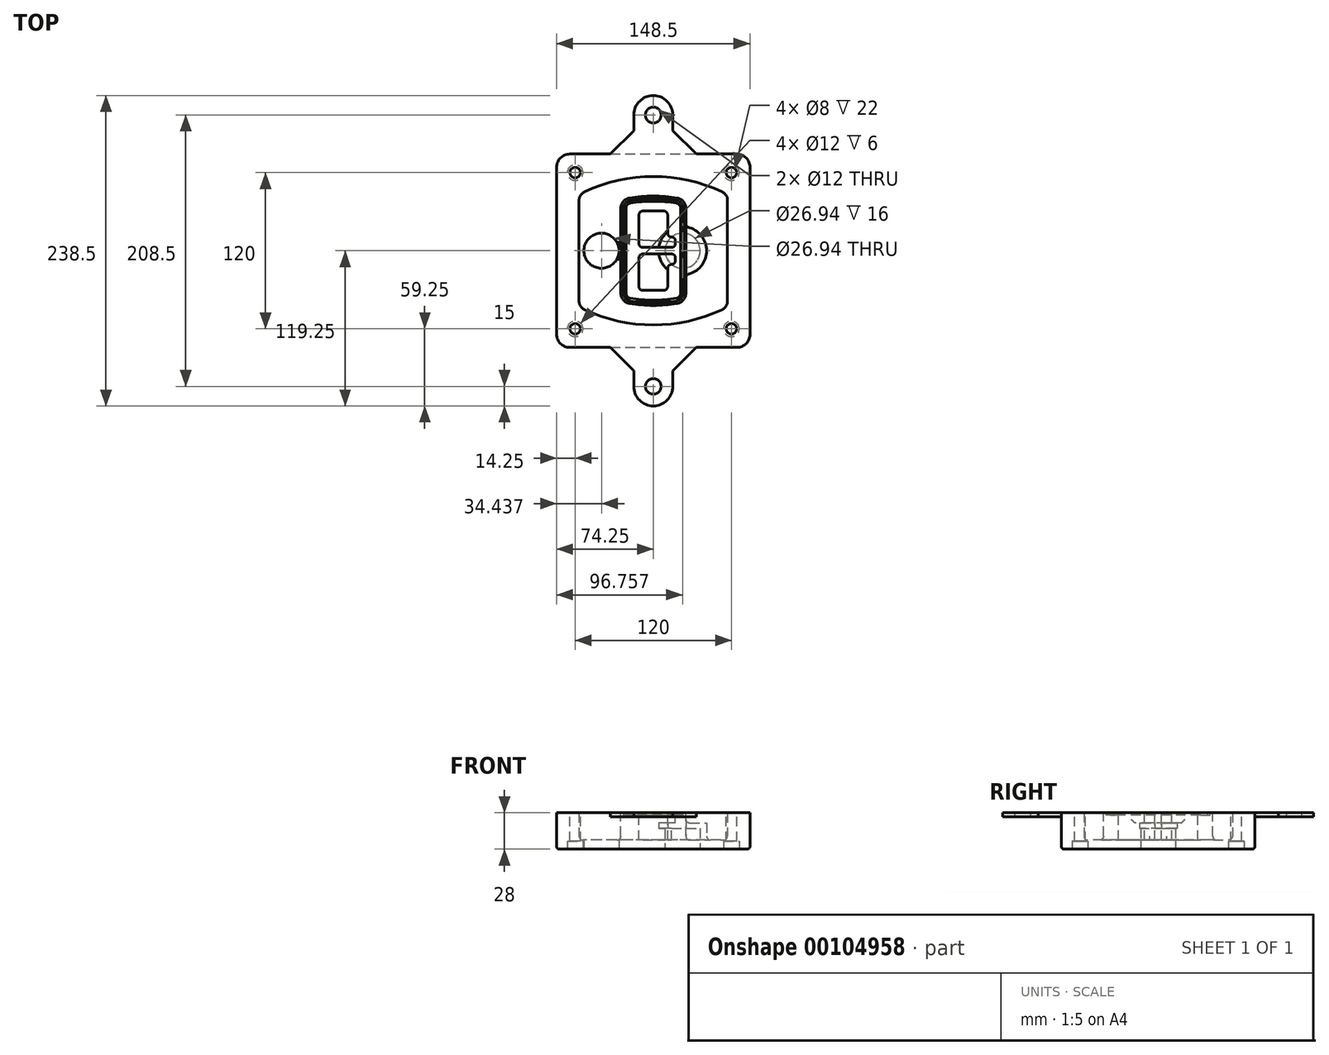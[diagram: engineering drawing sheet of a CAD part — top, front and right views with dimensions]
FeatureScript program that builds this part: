
annotation { "Feature Type Name" : "Feature", "Feature Type Description" : "" }
export const myFeature = defineFeature(function(context is Context, id is Id, definition is map)
    precondition{}
    {
        {
            var Q0;
            Q0=qCreatedBy(makeId("Top.planeOp"),FACE);
            var sketch = newSketch(context, id + "F0", { "sketchPlane" : qUnion([Q0])});
            skPoint(sketch, "E0.rect.middle", {"position": v(0, 0) * mm});
            skLineSegment(sketch, "E1.bottom", {"start": v(-64.25, -74.25) * mm, "end": v(64.25, -74.25) * mm});
            skLineSegment(sketch, "E1.top", {"start": v(-64.25, 74.25) * mm, "end": v(64.25, 74.25) * mm});
            skLineSegment(sketch, "E1.left", {"start": v(-74.25, -64.25) * mm, "end": v(-74.25, 64.25) * mm});
            skLineSegment(sketch, "E1.right", {"start": v(74.25, -64.25) * mm, "end": v(74.25, 64.25) * mm});
            skLineSegment(sketch, "E2", {"start": v(-74.25, 74.25) * mm, "end": v(74.25, -74.25) * mm, "construction": true});
            skLineSegment(sketch, "E3", {"start": v(74.25, 74.25) * mm, "end": v(-74.25, -74.25) * mm, "construction": true});
            skCircle(sketch, "E4", {"center": v(-60, 60) * mm, "radius": 4 * mm});
            skCircle(sketch, "E5", {"center": v(60, 60) * mm, "radius": 4 * mm});
            skCircle(sketch, "E6", {"center": v(60, -60) * mm, "radius": 4 * mm});
            skCircle(sketch, "E7", {"center": v(-60, -60) * mm, "radius": 4 * mm});
            skLineSegment(sketch, "E8", {"start": v(-60, 60) * mm, "end": v(60, 60) * mm, "construction": true});
            skLineSegment(sketch, "E9", {"start": v(60, 60) * mm, "end": v(60, -60) * mm, "construction": true});
            skLineSegment(sketch, "E10", {"start": v(60, -60) * mm, "end": v(-60, -60) * mm, "construction": true});
            skLineSegment(sketch, "E11", {"start": v(-60, -60) * mm, "end": v(-60, 60) * mm, "construction": true});
            skLineSegment(sketch, "E12", {"start": v(-60, 38.83) * mm, "end": v(-60, -38.83) * mm});
            skLineSegment(sketch, "E13", {"start": v(60, 38.83) * mm, "end": v(60, -38.83) * mm});
            skArc(sketch, "E14", {"start": v(54.26, 47.88) * mm, "mid": v(0, 60) * mm, "end": v(-54.26, 47.88) * mm});
            skArc(sketch, "E15", {"start": v(-54.26, -47.88) * mm, "mid": v(0, -60) * mm, "end": v(54.26, -47.88) * mm});
            skLineSegment(sketch, "E16", {"start": v(-60, 0) * mm, "end": v(60, 0) * mm, "construction": true});
            skPoint(sketch, "E17.visualSharp", {"position": v(-60, -45) * mm});
            skArc(sketch, "E17.filletArc", {"start": v(-60, -38.83) * mm, "mid": v(-58.44, -44.2) * mm, "end": v(-54.26, -47.88) * mm});
            skPoint(sketch, "E18.visualSharp", {"position": v(-60, 45) * mm});
            skArc(sketch, "E18.filletArc", {"start": v(-54.26, 47.88) * mm, "mid": v(-58.44, 44.2) * mm, "end": v(-60, 38.83) * mm});
            skPoint(sketch, "E19.visualSharp", {"position": v(60, 45) * mm});
            skArc(sketch, "E19.filletArc", {"start": v(60, 38.83) * mm, "mid": v(58.44, 44.2) * mm, "end": v(54.26, 47.88) * mm});
            skPoint(sketch, "E20.visualSharp", {"position": v(60, -45) * mm});
            skArc(sketch, "E20.filletArc", {"start": v(54.26, -47.88) * mm, "mid": v(58.44, -44.2) * mm, "end": v(60, -38.83) * mm});
            skPoint(sketch, "E21.visualSharp", {"position": v(-74.25, 74.25) * mm});
            skArc(sketch, "E21.filletArc", {"start": v(-64.25, 74.25) * mm, "mid": v(-71.32, 71.32) * mm, "end": v(-74.25, 64.25) * mm});
            skPoint(sketch, "E22.visualSharp", {"position": v(74.25, 74.25) * mm});
            skArc(sketch, "E22.filletArc", {"start": v(74.25, 64.25) * mm, "mid": v(71.32, 71.32) * mm, "end": v(64.25, 74.25) * mm});
            skPoint(sketch, "E23.visualSharp", {"position": v(74.25, -74.25) * mm});
            skArc(sketch, "E23.filletArc", {"start": v(64.25, -74.25) * mm, "mid": v(71.32, -71.32) * mm, "end": v(74.25, -64.25) * mm});
            skPoint(sketch, "E24.visualSharp", {"position": v(-74.25, -74.25) * mm});
            skArc(sketch, "E24.filletArc", {"start": v(-74.25, -64.25) * mm, "mid": v(-71.32, -71.32) * mm, "end": v(-64.25, -74.25) * mm});
            skArc(sketch, "E25.0", {"start": v(57, 38.83) * mm, "mid": v(55.9, 42.58) * mm, "end": v(52.98, 45.17) * mm});
            skLineSegment(sketch, "E25.1", {"start": v(57, 38.83) * mm, "end": v(57, -38.83) * mm});
            skArc(sketch, "E25.2", {"start": v(52.98, -45.17) * mm, "mid": v(55.9, -42.58) * mm, "end": v(57, -38.83) * mm});
            skArc(sketch, "E25.3", {"start": v(-52.98, -45.17) * mm, "mid": v(0, -57) * mm, "end": v(52.98, -45.17) * mm});
            skArc(sketch, "E25.4", {"start": v(-57, -38.83) * mm, "mid": v(-55.9, -42.58) * mm, "end": v(-52.98, -45.17) * mm});
            skArc(sketch, "E25.5", {"start": v(52.98, 45.17) * mm, "mid": v(0, 57) * mm, "end": v(-52.98, 45.17) * mm});
            skLineSegment(sketch, "E25.6", {"start": v(-57, 38.83) * mm, "end": v(-57, -38.83) * mm});
            skArc(sketch, "E25.7", {"start": v(-52.98, 45.17) * mm, "mid": v(-55.9, 42.58) * mm, "end": v(-57, 38.83) * mm});
            skArc(sketch, "E26.0", {"start": v(-55.96, 51.5) * mm, "mid": v(-61.82, 46.33) * mm, "end": v(-64, 38.83) * mm});
            skArc(sketch, "E26.1", {"start": v(55.96, 51.5) * mm, "mid": v(0, 64) * mm, "end": v(-55.96, 51.5) * mm});
            skArc(sketch, "E26.2", {"start": v(64, 38.83) * mm, "mid": v(61.82, 46.33) * mm, "end": v(55.96, 51.5) * mm});
            skLineSegment(sketch, "E26.3", {"start": v(64, 38.83) * mm, "end": v(64, -38.83) * mm});
            skArc(sketch, "E26.4", {"start": v(55.96, -51.5) * mm, "mid": v(61.82, -46.33) * mm, "end": v(64, -38.83) * mm});
            skLineSegment(sketch, "E26.5", {"start": v(-64, 38.83) * mm, "end": v(-64, -38.83) * mm});
            skArc(sketch, "E26.6", {"start": v(-55.96, -51.5) * mm, "mid": v(0, -64) * mm, "end": v(55.96, -51.5) * mm});
            skArc(sketch, "E26.7", {"start": v(-64, -38.83) * mm, "mid": v(-61.82, -46.33) * mm, "end": v(-55.96, -51.5) * mm});
            skSolve(sketch);
        }
        {
            var Q0;
            Q0=makeQuery(id+"F0.imprint","IMPRINT",FACE,{"disambiguationData":[TD([[makeQuery(id+"F0.imprint","IMPRINT",EDGE,{"derivedFrom":sQuery(id+"F0.wireOp",EDGE,"E1.bottom")}),1.0]])]});
            var Q1;
            Q1=makeQuery(id+"F0.imprint","IMPRINT",FACE,{"disambiguationData":[TD([[makeQuery(id+"F0.imprint","IMPRINT",EDGE,{"derivedFrom":sQuery(id+"F0.wireOp",EDGE,"E12")}),1.0]])]});
            var Q2;
            Q2=makeQuery(id+"F0.imprint","IMPRINT",FACE,{"disambiguationData":[TD([[makeQuery(id+"F0.imprint","IMPRINT",EDGE,{"derivedFrom":sQuery(id+"F0.wireOp",EDGE,"E25.0")}),1.0]])]});
            var Q3;
            Q3=makeQuery(id+"F0.imprint","IMPRINT",FACE,{"disambiguationData":[TD([[makeQuery(id+"F0.imprint","IMPRINT",EDGE,{"derivedFrom":sQuery(id+"F0.wireOp",EDGE,"E12")}),-1.0]])]});
            extrude(context, id + "F1", {"entities" : qUnion([Q0, Q1, Q2, Q3]), "oppositeDirection" : true, "depth" : 25 * mm});
        }
        {
            var Q0;
            Q0=makeQuery(id+"F0.imprint","IMPRINT",FACE,{"disambiguationData":[TD([[makeQuery(id+"F0.imprint","IMPRINT",EDGE,{"derivedFrom":sQuery(id+"F0.wireOp",EDGE,"E12")}),1.0]])]});
            extrude(context, id + "F2", {"entities" : qUnion([Q0]), "operationType" : NewBodyOperationType.ADD, "depth" : 3 * mm});
        }
        {
            var Q0;
            Q0=makeQuery(id+"F0.imprint","IMPRINT",FACE,{"disambiguationData":[TD([[makeQuery(id+"F0.imprint","IMPRINT",EDGE,{"derivedFrom":sQuery(id+"F0.wireOp",EDGE,"E25.0")}),1.0]])]});
            extrude(context, id + "F3", {"entities" : qUnion([Q0]), "operationType" : NewBodyOperationType.REMOVE, "oppositeDirection" : true, "depth" : 18 * mm});
        }
        {
            var Q0;
            Q0=makeQuery(id+"F2.opExtrude","CAP_FACE",FACE,{"disambiguationData":[OSD([sQuery(id+"F0.wireOp",EDGE,"E12"),sQuery(id+"F0.wireOp",EDGE,"E13"),sQuery(id+"F0.wireOp",EDGE,"E14"),sQuery(id+"F0.wireOp",EDGE,"E15"),sQuery(id+"F0.wireOp",EDGE,"E17.filletArc"),sQuery(id+"F0.wireOp",EDGE,"E18.filletArc"),sQuery(id+"F0.wireOp",EDGE,"E19.filletArc"),sQuery(id+"F0.wireOp",EDGE,"E20.filletArc"),sQuery(id+"F0.wireOp",EDGE,"E25.0"),sQuery(id+"F0.wireOp",EDGE,"E25.1"),sQuery(id+"F0.wireOp",EDGE,"E25.2"),sQuery(id+"F0.wireOp",EDGE,"E25.3"),sQuery(id+"F0.wireOp",EDGE,"E25.4"),sQuery(id+"F0.wireOp",EDGE,"E25.5"),sQuery(id+"F0.wireOp",EDGE,"E25.6"),sQuery(id+"F0.wireOp",EDGE,"E25.7")])],"isStart":false});
            var sketch = newSketch(context, id + "F4", { "sketchPlane" : qUnion([Q0])});
            skArc(sketch, "E27.0", {"start": v(-18.34, -40.45) * mm, "mid": v(0, -42) * mm, "end": v(18.34, -40.45) * mm});
            skArc(sketch, "E28.0", {"start": v(18.34, 40.45) * mm, "mid": v(0, 42) * mm, "end": v(-18.34, 40.45) * mm});
            skLineSegment(sketch, "E29", {"start": v(-25, 32.57) * mm, "end": v(-25, -32.57) * mm});
            skLineSegment(sketch, "E30", {"start": v(25, 32.57) * mm, "end": v(25, -32.57) * mm});
            skLineSegment(sketch, "E31", {"start": v(-25, 39.1) * mm, "end": v(25, 39.1) * mm, "construction": true});
            skLineSegment(sketch, "E32", {"start": v(-25, -39.1) * mm, "end": v(25, -39.1) * mm, "construction": true});
            skPoint(sketch, "E33.visualSharp", {"position": v(-25, 39.1) * mm});
            skArc(sketch, "E33.filletArc", {"start": v(-18.34, 40.45) * mm, "mid": v(-23.11, 37.73) * mm, "end": v(-25, 32.57) * mm});
            skPoint(sketch, "E34.visualSharp", {"position": v(25, 39.1) * mm});
            skArc(sketch, "E34.filletArc", {"start": v(25, 32.57) * mm, "mid": v(23.11, 37.73) * mm, "end": v(18.34, 40.45) * mm});
            skPoint(sketch, "E35.visualSharp", {"position": v(25, -39.1) * mm});
            skArc(sketch, "E35.filletArc", {"start": v(18.34, -40.45) * mm, "mid": v(23.11, -37.73) * mm, "end": v(25, -32.57) * mm});
            skPoint(sketch, "E36.visualSharp", {"position": v(-25, -39.1) * mm});
            skArc(sketch, "E36.filletArc", {"start": v(-25, -32.57) * mm, "mid": v(-23.11, -37.73) * mm, "end": v(-18.34, -40.45) * mm});
            skArc(sketch, "E37.0", {"start": v(52.98, 45.17) * mm, "mid": v(0, 57) * mm, "end": v(-52.98, 45.17) * mm});
            skArc(sketch, "E37.1", {"start": v(-52.98, 45.17) * mm, "mid": v(-55.9, 42.58) * mm, "end": v(-57, 38.83) * mm});
            skLineSegment(sketch, "E37.2", {"start": v(-57, 38.83) * mm, "end": v(-57, -38.83) * mm});
            skArc(sketch, "E37.3", {"start": v(-57, -38.83) * mm, "mid": v(-55.9, -42.58) * mm, "end": v(-52.98, -45.17) * mm});
            skArc(sketch, "E37.4", {"start": v(-52.98, -45.17) * mm, "mid": v(0, -57) * mm, "end": v(52.98, -45.17) * mm});
            skArc(sketch, "E37.5", {"start": v(52.98, -45.17) * mm, "mid": v(55.9, -42.58) * mm, "end": v(57, -38.83) * mm});
            skLineSegment(sketch, "E37.6", {"start": v(57, 38.83) * mm, "end": v(57, -38.83) * mm});
            skArc(sketch, "E37.7", {"start": v(57, 38.83) * mm, "mid": v(55.9, 42.58) * mm, "end": v(52.98, 45.17) * mm});
            skLineSegment(sketch, "E38.0", {"start": v(23, 32.57) * mm, "end": v(23, -32.57) * mm});
            skArc(sketch, "E38.1", {"start": v(18, -38.48) * mm, "mid": v(21.58, -36.44) * mm, "end": v(23, -32.57) * mm});
            skArc(sketch, "E38.2", {"start": v(-18, -38.48) * mm, "mid": v(0, -40) * mm, "end": v(18, -38.48) * mm});
            skArc(sketch, "E38.3", {"start": v(-23, -32.57) * mm, "mid": v(-21.58, -36.44) * mm, "end": v(-18, -38.48) * mm});
            skLineSegment(sketch, "E38.4", {"start": v(-23, 32.57) * mm, "end": v(-23, -32.57) * mm});
            skArc(sketch, "E38.5", {"start": v(23, 32.57) * mm, "mid": v(21.58, 36.44) * mm, "end": v(18, 38.48) * mm});
            skArc(sketch, "E38.6", {"start": v(-18, 38.48) * mm, "mid": v(-21.58, 36.44) * mm, "end": v(-23, 32.57) * mm});
            skArc(sketch, "E38.7", {"start": v(18, 38.48) * mm, "mid": v(0, 40) * mm, "end": v(-18, 38.48) * mm});
            skArc(sketch, "E39.0", {"start": v(21, 32.57) * mm, "mid": v(20.06, 35.15) * mm, "end": v(17.67, 36.5) * mm});
            skLineSegment(sketch, "E39.1", {"start": v(21, 32.57) * mm, "end": v(21, -32.57) * mm});
            skArc(sketch, "E39.2", {"start": v(17.67, -36.5) * mm, "mid": v(20.06, -35.15) * mm, "end": v(21, -32.57) * mm});
            skArc(sketch, "E39.3", {"start": v(-17.67, -36.5) * mm, "mid": v(0, -38) * mm, "end": v(17.67, -36.5) * mm});
            skArc(sketch, "E39.4", {"start": v(-21, -32.57) * mm, "mid": v(-20.06, -35.15) * mm, "end": v(-17.67, -36.5) * mm});
            skArc(sketch, "E39.5", {"start": v(17.67, 36.5) * mm, "mid": v(0, 38) * mm, "end": v(-17.67, 36.5) * mm});
            skLineSegment(sketch, "E39.6", {"start": v(-21, 32.57) * mm, "end": v(-21, -32.57) * mm});
            skArc(sketch, "E39.7", {"start": v(-17.67, 36.5) * mm, "mid": v(-20.06, 35.15) * mm, "end": v(-21, 32.57) * mm});
            skLineSegment(sketch, "E40", {"start": v(-25, 0) * mm, "end": v(25, 0) * mm, "construction": true});
            skLineSegment(sketch, "E41", {"start": v(-11, 5.5) * mm, "end": v(-11, 27.5) * mm});
            skLineSegment(sketch, "E42", {"start": v(-8, 30.5) * mm, "end": v(8, 30.5) * mm});
            skLineSegment(sketch, "E43", {"start": v(11, 27.5) * mm, "end": v(11, 13.5) * mm});
            skLineSegment(sketch, "E44", {"start": v(14, 10.5) * mm, "end": v(14, 10.5) * mm});
            skLineSegment(sketch, "E45", {"start": v(17, 7.5) * mm, "end": v(17, 5.5) * mm});
            skLineSegment(sketch, "E46", {"start": v(14, 2.5) * mm, "end": v(-8, 2.5) * mm});
            skPoint(sketch, "E47.visualSharp", {"position": v(-11, 30.5) * mm});
            skArc(sketch, "E47.filletArc", {"start": v(-8, 30.5) * mm, "mid": v(-10.12, 29.62) * mm, "end": v(-11, 27.5) * mm});
            skPoint(sketch, "E48.visualSharp", {"position": v(11, 30.5) * mm});
            skArc(sketch, "E48.filletArc", {"start": v(11, 27.5) * mm, "mid": v(10.12, 29.62) * mm, "end": v(8, 30.5) * mm});
            skPoint(sketch, "E49.visualSharp", {"position": v(11, 10.5) * mm});
            skArc(sketch, "E49.filletArc", {"start": v(11, 13.5) * mm, "mid": v(11.88, 11.38) * mm, "end": v(14, 10.5) * mm});
            skPoint(sketch, "E50.visualSharp", {"position": v(17, 10.5) * mm});
            skArc(sketch, "E50.filletArc", {"start": v(17, 7.5) * mm, "mid": v(16.12, 9.62) * mm, "end": v(14, 10.5) * mm});
            skPoint(sketch, "E51.visualSharp", {"position": v(17, 2.5) * mm});
            skArc(sketch, "E51.filletArc", {"start": v(14, 2.5) * mm, "mid": v(16.12, 3.38) * mm, "end": v(17, 5.5) * mm});
            skPoint(sketch, "E52.visualSharp", {"position": v(-11, 2.5) * mm});
            skArc(sketch, "E52.filletArc", {"start": v(-11, 5.5) * mm, "mid": v(-10.12, 3.38) * mm, "end": v(-8, 2.5) * mm});
            skLineSegment(sketch, "E53.0.MirrorCS", {"start": v(14, -2.5) * mm, "end": v(-8, -2.5) * mm});
            skArc(sketch, "E54.0.MirrorCS", {"start": v(-11, -5.5) * mm, "mid": v(-10.12, -3.38) * mm, "end": v(-8, -2.5) * mm});
            skLineSegment(sketch, "E55.0.MirrorCS", {"start": v(-11, -5.5) * mm, "end": v(-11, -27.5) * mm});
            skArc(sketch, "E56.0.MirrorCS", {"start": v(-8, -30.5) * mm, "mid": v(-10.12, -29.62) * mm, "end": v(-11, -27.5) * mm});
            skLineSegment(sketch, "E57.0.MirrorCS", {"start": v(-8, -30.5) * mm, "end": v(8, -30.5) * mm});
            skArc(sketch, "E58.0.MirrorCS", {"start": v(11, -27.5) * mm, "mid": v(10.12, -29.62) * mm, "end": v(8, -30.5) * mm});
            skLineSegment(sketch, "E59.0.MirrorCS", {"start": v(11, -27.5) * mm, "end": v(11, -13.5) * mm});
            skArc(sketch, "E60.0.MirrorCS", {"start": v(11, -13.5) * mm, "mid": v(11.88, -11.38) * mm, "end": v(14, -10.5) * mm});
            skArc(sketch, "E61.0.MirrorCS", {"start": v(17, -7.5) * mm, "mid": v(16.12, -9.62) * mm, "end": v(14, -10.5) * mm});
            skLineSegment(sketch, "E62.0.MirrorCS", {"start": v(17, -7.5) * mm, "end": v(17, -5.5) * mm});
            skArc(sketch, "E63.0.MirrorCS", {"start": v(14, -2.5) * mm, "mid": v(16.12, -3.38) * mm, "end": v(17, -5.5) * mm});
            skSolve(sketch);
        }
        {
            var Q0;
            Q0=makeQuery(id+"F4.imprint","IMPRINT",FACE,{"disambiguationData":[TD([[makeQuery(id+"F4.imprint","IMPRINT",EDGE,{"derivedFrom":sQuery(id+"F4.wireOp",EDGE,"E27.0")}),1.0]])]});
            var Q1;
            Q1=makeQuery(id+"F4.imprint","IMPRINT",FACE,{"disambiguationData":[TD([[makeQuery(id+"F4.imprint","IMPRINT",EDGE,{"derivedFrom":sQuery(id+"F4.wireOp",EDGE,"E38.0")}),-1.0]])]});
            var Q2;
            Q2=makeQuery(id+"F4.imprint","IMPRINT",FACE,{"disambiguationData":[TD([[makeQuery(id+"F4.imprint","IMPRINT",EDGE,{"derivedFrom":sQuery(id+"F4.wireOp",EDGE,"E39.0")}),1.0]])]});
            extrude(context, id + "F5", {"entities" : qUnion([Q0, Q1, Q2]), "operationType" : NewBodyOperationType.ADD, "endBound" : BoundingType.UP_TO_NEXT, "oppositeDirection" : true, "depth" : 25 * mm});
        }
        {
            var Q0;
            Q0=makeQuery(id+"F4.imprint","IMPRINT",FACE,{"disambiguationData":[TD([[makeQuery(id+"F4.imprint","IMPRINT",EDGE,{"derivedFrom":sQuery(id+"F4.wireOp",EDGE,"E38.0")}),-1.0]])]});
            extrude(context, id + "F6", {"entities" : qUnion([Q0]), "operationType" : NewBodyOperationType.REMOVE, "oppositeDirection" : true, "depth" : 2 * mm});
        }
        {
            var Q0;
            Q0=makeQuery(id+"F1.opExtrude","CAP_FACE",FACE,{"disambiguationData":[OSD([sQuery(id+"F0.wireOp",EDGE,"E1.bottom"),sQuery(id+"F0.wireOp",EDGE,"E1.top"),sQuery(id+"F0.wireOp",EDGE,"E1.left"),sQuery(id+"F0.wireOp",EDGE,"E1.right"),sQuery(id+"F0.wireOp",EDGE,"E4"),sQuery(id+"F0.wireOp",EDGE,"E5"),sQuery(id+"F0.wireOp",EDGE,"E6"),sQuery(id+"F0.wireOp",EDGE,"E7"),sQuery(id+"F0.wireOp",EDGE,"E21.filletArc"),sQuery(id+"F0.wireOp",EDGE,"E22.filletArc"),sQuery(id+"F0.wireOp",EDGE,"E23.filletArc"),sQuery(id+"F0.wireOp",EDGE,"E24.filletArc")])],"isStart":false});
            var sketch = newSketch(context, id + "F7", { "sketchPlane" : qUnion([Q0])});
            skCircle(sketch, "E64", {"center": v(22.5, 0) * mm, "radius": 13.47 * mm});
            skCircle(sketch, "E65", {"center": v(-39.81, 0) * mm, "radius": 13.47 * mm});
            skLineSegment(sketch, "E66", {"start": v(74.25, 0) * mm, "end": v(-74.25, 0) * mm});
            skCircle(sketch, "E67", {"center": v(22.5, 0) * mm, "radius": 18.47 * mm});
            skCircle(sketch, "E68", {"center": v(60, -60) * mm, "radius": 6 * mm});
            skCircle(sketch, "E69", {"center": v(-60, -60) * mm, "radius": 6 * mm});
            skCircle(sketch, "E70", {"center": v(-60, 60) * mm, "radius": 6 * mm});
            skCircle(sketch, "E71", {"center": v(60, 60) * mm, "radius": 6 * mm});
            skSolve(sketch);
        }
        {
            var Q0;
            {var subQ1=sQuery(id+"F7.wireOp",EDGE,"E66");var subQ4=sQuery(id+"F7.wireOp",EDGE,"E64");var subQ6=makeQuery(id+"F7.imprint","INTERSECT",VERTEX,{"disambiguationData":[OD(0.0)],"derivedFrom":[subQ4,subQ1]});Q0=makeQuery(id+"F7.imprint","IMPRINT",FACE,{"disambiguationData":[TD([[makeQuery(id+"F7.imprint","IMPRINT",EDGE,{"disambiguationData":[TD([[subQ6,-1.0]])],"derivedFrom":subQ4}),-1.0]])]});}
            var Q1;
            {var subQ0=sQuery(id+"F7.wireOp",EDGE,"E66");var subQ1=sQuery(id+"F7.wireOp",EDGE,"E64");var subQ3=makeQuery(id+"F7.imprint","INTERSECT",VERTEX,{"disambiguationData":[OD(0.0)],"derivedFrom":[subQ1,subQ0]});Q1=makeQuery(id+"F7.imprint","IMPRINT",FACE,{"disambiguationData":[TD([[makeQuery(id+"F7.imprint","IMPRINT",EDGE,{"disambiguationData":[TD([[subQ3,-1.0]])],"derivedFrom":subQ1}),1.0]])]});}
            var Q2;
            {var subQ0=sQuery(id+"F7.wireOp",EDGE,"E66");var subQ1=sQuery(id+"F7.wireOp",EDGE,"E64");var subQ3=makeQuery(id+"F7.imprint","INTERSECT",VERTEX,{"disambiguationData":[OD(0.0)],"derivedFrom":[subQ1,subQ0]});Q2=makeQuery(id+"F7.imprint","IMPRINT",FACE,{"disambiguationData":[TD([[makeQuery(id+"F7.imprint","IMPRINT",EDGE,{"disambiguationData":[TD([[subQ3,1.0]])],"derivedFrom":subQ1}),1.0]])]});}
            var Q3;
            {var subQ1=sQuery(id+"F7.wireOp",EDGE,"E66");var subQ4=sQuery(id+"F7.wireOp",EDGE,"E64");var subQ6=makeQuery(id+"F7.imprint","INTERSECT",VERTEX,{"disambiguationData":[OD(0.0)],"derivedFrom":[subQ4,subQ1]});Q3=makeQuery(id+"F7.imprint","IMPRINT",FACE,{"disambiguationData":[TD([[makeQuery(id+"F7.imprint","IMPRINT",EDGE,{"disambiguationData":[TD([[subQ6,1.0]])],"derivedFrom":subQ4}),-1.0]])]});}
            extrude(context, id + "F8", {"entities" : qUnion([Q0, Q1, Q2, Q3]), "operationType" : NewBodyOperationType.ADD, "oppositeDirection" : true, "depth" : 20 * mm});
        }
        {
            var Q0;
            {var subQ0=sQuery(id+"F7.wireOp",EDGE,"E66");var subQ1=sQuery(id+"F7.wireOp",EDGE,"E64");var subQ3=makeQuery(id+"F7.imprint","INTERSECT",VERTEX,{"disambiguationData":[OD(0.0)],"derivedFrom":[subQ1,subQ0]});Q0=makeQuery(id+"F7.imprint","IMPRINT",FACE,{"disambiguationData":[TD([[makeQuery(id+"F7.imprint","IMPRINT",EDGE,{"disambiguationData":[TD([[subQ3,-1.0]])],"derivedFrom":subQ1}),1.0]])]});}
            var Q1;
            {var subQ0=sQuery(id+"F7.wireOp",EDGE,"E66");var subQ1=sQuery(id+"F7.wireOp",EDGE,"E64");var subQ3=makeQuery(id+"F7.imprint","INTERSECT",VERTEX,{"disambiguationData":[OD(0.0)],"derivedFrom":[subQ1,subQ0]});Q1=makeQuery(id+"F7.imprint","IMPRINT",FACE,{"disambiguationData":[TD([[makeQuery(id+"F7.imprint","IMPRINT",EDGE,{"disambiguationData":[TD([[subQ3,1.0]])],"derivedFrom":subQ1}),1.0]])]});}
            extrude(context, id + "F9", {"entities" : qUnion([Q0, Q1]), "operationType" : NewBodyOperationType.REMOVE, "oppositeDirection" : true, "depth" : 16 * mm});
        }
        {
            var Q0;
            {var subQ0=sQuery(id+"F7.wireOp",EDGE,"E66");var subQ1=sQuery(id+"F7.wireOp",EDGE,"E65");var subQ3=makeQuery(id+"F7.imprint","INTERSECT",VERTEX,{"disambiguationData":[OD(0.0)],"derivedFrom":[subQ1,subQ0]});Q0=makeQuery(id+"F7.imprint","IMPRINT",FACE,{"disambiguationData":[TD([[makeQuery(id+"F7.imprint","IMPRINT",EDGE,{"disambiguationData":[TD([[subQ3,-1.0]])],"derivedFrom":subQ1}),1.0]])]});}
            var Q1;
            {var subQ0=sQuery(id+"F7.wireOp",EDGE,"E66");var subQ1=sQuery(id+"F7.wireOp",EDGE,"E65");var subQ3=makeQuery(id+"F7.imprint","INTERSECT",VERTEX,{"disambiguationData":[OD(0.0)],"derivedFrom":[subQ1,subQ0]});Q1=makeQuery(id+"F7.imprint","IMPRINT",FACE,{"disambiguationData":[TD([[makeQuery(id+"F7.imprint","IMPRINT",EDGE,{"disambiguationData":[TD([[subQ3,1.0]])],"derivedFrom":subQ1}),1.0]])]});}
            extrude(context, id + "F10", {"entities" : qUnion([Q0, Q1]), "operationType" : NewBodyOperationType.REMOVE, "oppositeDirection" : true, "depth" : 25 * mm});
        }
        {
            var Q0;
            Q0=makeQuery(id+"F7.imprint","IMPRINT",FACE,{"disambiguationData":[TD([[makeQuery(id+"F7.imprint","IMPRINT",EDGE,{"derivedFrom":sQuery(id+"F7.wireOp",EDGE,"E68")}),1.0]])]});
            var Q1;
            Q1=makeQuery(id+"F7.imprint","IMPRINT",FACE,{"disambiguationData":[TD([[makeQuery(id+"F7.imprint","IMPRINT",EDGE,{"derivedFrom":makeQuery(id+"F1.opExtrude","CAP_EDGE",EDGE,{"disambiguationData":[OSD([sQuery(id+"F0.wireOp",EDGE,"E5")])],"isStart":false})}),-1.0]])]});
            var Q2;
            Q2=makeQuery(id+"F7.imprint","IMPRINT",FACE,{"disambiguationData":[TD([[makeQuery(id+"F7.imprint","IMPRINT",EDGE,{"derivedFrom":sQuery(id+"F7.wireOp",EDGE,"E69")}),1.0]])]});
            var Q3;
            Q3=makeQuery(id+"F7.imprint","IMPRINT",FACE,{"disambiguationData":[TD([[makeQuery(id+"F7.imprint","IMPRINT",EDGE,{"derivedFrom":makeQuery(id+"F1.opExtrude","CAP_EDGE",EDGE,{"disambiguationData":[OSD([sQuery(id+"F0.wireOp",EDGE,"E4")])],"isStart":false})}),-1.0]])]});
            var Q4;
            Q4=makeQuery(id+"F7.imprint","IMPRINT",FACE,{"disambiguationData":[TD([[makeQuery(id+"F7.imprint","IMPRINT",EDGE,{"derivedFrom":sQuery(id+"F7.wireOp",EDGE,"E70")}),1.0]])]});
            var Q5;
            Q5=makeQuery(id+"F7.imprint","IMPRINT",FACE,{"disambiguationData":[TD([[makeQuery(id+"F7.imprint","IMPRINT",EDGE,{"derivedFrom":makeQuery(id+"F1.opExtrude","CAP_EDGE",EDGE,{"disambiguationData":[OSD([sQuery(id+"F0.wireOp",EDGE,"E7")])],"isStart":false})}),-1.0]])]});
            var Q6;
            Q6=makeQuery(id+"F7.imprint","IMPRINT",FACE,{"disambiguationData":[TD([[makeQuery(id+"F7.imprint","IMPRINT",EDGE,{"derivedFrom":sQuery(id+"F7.wireOp",EDGE,"E71")}),1.0]])]});
            var Q7;
            Q7=makeQuery(id+"F7.imprint","IMPRINT",FACE,{"disambiguationData":[TD([[makeQuery(id+"F7.imprint","IMPRINT",EDGE,{"derivedFrom":makeQuery(id+"F1.opExtrude","CAP_EDGE",EDGE,{"disambiguationData":[OSD([sQuery(id+"F0.wireOp",EDGE,"E6")])],"isStart":false})}),-1.0]])]});
            extrude(context, id + "F11", {"entities" : qUnion([Q0, Q1, Q2, Q3, Q4, Q5, Q6, Q7]), "operationType" : NewBodyOperationType.REMOVE, "oppositeDirection" : true, "depth" : 6 * mm});
        }
        {
            var Q0;
            Q0=makeQuery(id+"F9.boolean.opBoolean","COPY",FACE,{"derivedFrom":makeQuery(id+"F9.opExtrude","CAP_FACE",FACE,{"disambiguationData":[OSD([sQuery(id+"F7.wireOp",EDGE,"E64")])],"isStart":false})});
            var sketch = newSketch(context, id + "F12", { "sketchPlane" : qUnion([Q0])});
            skArc(sketch, "E72.0", {"start": v(11, 14.45) * mm, "mid": v(6.45, 9.13) * mm, "end": v(4.2, 2.5) * mm});
            skArc(sketch, "E72.1", {"start": v(4.2, -2.5) * mm, "mid": v(6.45, -9.13) * mm, "end": v(11, -14.45) * mm});
            skLineSegment(sketch, "E73", {"start": v(4.2, -2.5) * mm, "end": v(14, -2.5) * mm});
            skLineSegment(sketch, "E74.0", {"start": v(14, 2.5) * mm, "end": v(4.2, 2.5) * mm});
            skArc(sketch, "E74.1", {"start": v(14, 2.5) * mm, "mid": v(16.12, 3.38) * mm, "end": v(17, 5.5) * mm});
            skLineSegment(sketch, "E74.2", {"start": v(17, 7.5) * mm, "end": v(17, 5.5) * mm});
            skArc(sketch, "E74.3", {"start": v(17, 7.5) * mm, "mid": v(16.12, 9.62) * mm, "end": v(14, 10.5) * mm});
            skArc(sketch, "E74.4", {"start": v(11, 13.5) * mm, "mid": v(11.88, 11.38) * mm, "end": v(14, 10.5) * mm});
            skLineSegment(sketch, "E74.5", {"start": v(11, 14.45) * mm, "end": v(11, 13.5) * mm});
            skLineSegment(sketch, "E74.7", {"start": v(14, -2.5) * mm, "end": v(4.2, -2.5) * mm});
            skArc(sketch, "E74.8", {"start": v(14, -2.5) * mm, "mid": v(16.12, -3.38) * mm, "end": v(17, -5.5) * mm});
            skLineSegment(sketch, "E74.9", {"start": v(17, -7.5) * mm, "end": v(17, -5.5) * mm});
            skArc(sketch, "E74.10", {"start": v(17, -7.5) * mm, "mid": v(16.12, -9.62) * mm, "end": v(14, -10.5) * mm});
            skArc(sketch, "E74.11", {"start": v(11, -13.5) * mm, "mid": v(11.88, -11.38) * mm, "end": v(14, -10.5) * mm});
            skLineSegment(sketch, "E74.12", {"start": v(11, -14.45) * mm, "end": v(11, -13.5) * mm});
            skPoint(sketch, "E75.orphan", {"position": v(11, -27.5) * mm});
            skPoint(sketch, "E76.orphan", {"position": v(-8, -2.5) * mm});
            skPoint(sketch, "E77.orphan", {"position": v(-8, 2.5) * mm});
            skPoint(sketch, "E78.orphan", {"position": v(11, 27.5) * mm});
            skSolve(sketch);
        }
        {
            var Q0;
            {var subQ7=sQuery(id+"F12.wireOp",EDGE,"E72.0");var subQ14=sQuery(id+"F12.wireOp",EDGE,"E72.1");var subQ16=sQuery(id+"F12.wireOp",EDGE,"E74.1");var subQ18=sQuery(id+"F12.wireOp",EDGE,"E74.8");Q0=qUnion([makeQuery(id+"F12.imprint","IMPRINT",FACE,{"disambiguationData":[TD([[makeQuery(id+"F12.imprint","IMPRINT",EDGE,{"derivedFrom":subQ7}),1.0]])]}),makeQuery(id+"F12.imprint","IMPRINT",FACE,{"disambiguationData":[TD([[makeQuery(id+"F12.imprint","IMPRINT",EDGE,{"derivedFrom":subQ14}),1.0]])]}),makeQuery(id+"F12.imprint","IMPRINT",FACE,{"disambiguationData":[TD([[makeQuery(id+"F12.imprint","IMPRINT",EDGE,{"derivedFrom":subQ16}),1.0]])]}),makeQuery(id+"F12.imprint","IMPRINT",FACE,{"disambiguationData":[TD([[makeQuery(id+"F12.imprint","IMPRINT",EDGE,{"derivedFrom":subQ18}),-1.0]])]})]);}
            var Q1;
            Q1=makeQuery(id+"F5.boolean.opBoolean","SPLIT",FACE,{"disambiguationData":[TD([makeQuery(id+"F5.opExtrude","SWEPT_FACE",FACE,{"disambiguationData":[OSD([sQuery(id+"F4.wireOp",EDGE,"E41")])]})])],"derivedFrom":makeQuery(id+"F3.boolean.opBoolean","COPY",FACE,{"derivedFrom":makeQuery(id+"F3.opExtrude","CAP_FACE",FACE,{"disambiguationData":[OSD([sQuery(id+"F0.wireOp",EDGE,"E25.0"),sQuery(id+"F0.wireOp",EDGE,"E25.1"),sQuery(id+"F0.wireOp",EDGE,"E25.2"),sQuery(id+"F0.wireOp",EDGE,"E25.3"),sQuery(id+"F0.wireOp",EDGE,"E25.4"),sQuery(id+"F0.wireOp",EDGE,"E25.5"),sQuery(id+"F0.wireOp",EDGE,"E25.6"),sQuery(id+"F0.wireOp",EDGE,"E25.7")])],"isStart":false})})});
            extrude(context, id + "F13", {"entities" : qUnion([Q0]), "operationType" : NewBodyOperationType.REMOVE, "endBound" : BoundingType.UP_TO_SURFACE, "endBoundEntityFace" : qUnion([Q1]), "depth" : 25 * mm});
        }
        {
            var Q0;
            Q0=makeQuery(id+"F3.boolean.opBoolean","COPY",EDGE,{"derivedFrom":makeQuery(id+"F3.opExtrude","CAP_EDGE",EDGE,{"disambiguationData":[OSD([sQuery(id+"F0.wireOp",EDGE,"E25.6")])],"isStart":false})});
            var Q1;
            Q1=makeQuery(id+"F8.boolean.opBoolean","INTERSECT",EDGE,{"derivedFrom":[makeQuery(id+"F5.opExtrude","SWEPT_FACE",FACE,{"disambiguationData":[OSD([sQuery(id+"F4.wireOp",EDGE,"E30")])]}),makeQuery(id+"F8.opExtrude","CAP_FACE",FACE,{"disambiguationData":[OSD([sQuery(id+"F7.wireOp",EDGE,"E67")])],"isStart":false})]});
            var Q2;
            Q2=makeQuery(id+"F8.boolean.opBoolean","INTERSECT",EDGE,{"disambiguationData":[OD(1.0)],"derivedFrom":[makeQuery(id+"F5.opExtrude","SWEPT_FACE",FACE,{"disambiguationData":[OSD([sQuery(id+"F4.wireOp",EDGE,"E30")])]}),makeQuery(id+"F8.opExtrude","SWEPT_FACE",FACE,{"disambiguationData":[OSD([sQuery(id+"F7.wireOp",EDGE,"E67")])]})]});
            var Q3;
            {var subQ0=sQuery(id+"F4.wireOp",EDGE,"E30");Q3=makeQuery(id+"F8.boolean.opBoolean","SPLIT",EDGE,{"disambiguationData":[TD([makeQuery(id+"F5.opExtrude","SWEPT_FACE",FACE,{"disambiguationData":[OSD([sQuery(id+"F4.wireOp",EDGE,"E35.filletArc")])]})])],"derivedFrom":makeQuery(id+"F5.opExtrude","CAP_EDGE",EDGE,{"disambiguationData":[OSD([subQ0])],"isStart":false})});}
            var Q4;
            {var subQ0=sQuery(id+"F0.wireOp",EDGE,"E25.7");var subQ1=sQuery(id+"F0.wireOp",EDGE,"E25.1");var subQ2=sQuery(id+"F0.wireOp",EDGE,"E25.6");var subQ3=sQuery(id+"F0.wireOp",EDGE,"E25.5");var subQ4=sQuery(id+"F0.wireOp",EDGE,"E25.4");var subQ5=sQuery(id+"F0.wireOp",EDGE,"E25.0");var subQ6=sQuery(id+"F0.wireOp",EDGE,"E25.2");var subQ7=sQuery(id+"F0.wireOp",EDGE,"E25.3");Q4=makeQuery(id+"F8.boolean.opBoolean","INTERSECT",EDGE,{"derivedFrom":[makeQuery(id+"F5.boolean.opBoolean","SPLIT",FACE,{"disambiguationData":[TD([makeQuery(id+"F2.opExtrude","SWEPT_FACE",FACE,{"disambiguationData":[OSD([subQ5])]})])],"derivedFrom":makeQuery(id+"F3.boolean.opBoolean","COPY",FACE,{"derivedFrom":makeQuery(id+"F3.opExtrude","CAP_FACE",FACE,{"disambiguationData":[OSD([subQ5,subQ1,subQ6,subQ7,subQ4,subQ3,subQ2,subQ0])],"isStart":false})})}),makeQuery(id+"F8.opExtrude","SWEPT_FACE",FACE,{"disambiguationData":[OSD([sQuery(id+"F7.wireOp",EDGE,"E67")])]})]});}
            var Q5;
            Q5=makeQuery(id+"F8.boolean.opBoolean","INTERSECT",EDGE,{"disambiguationData":[OD(0.0)],"derivedFrom":[makeQuery(id+"F5.opExtrude","SWEPT_FACE",FACE,{"disambiguationData":[OSD([sQuery(id+"F4.wireOp",EDGE,"E30")])]}),makeQuery(id+"F8.opExtrude","SWEPT_FACE",FACE,{"disambiguationData":[OSD([sQuery(id+"F7.wireOp",EDGE,"E67")])]})]});
            fillet(context, id + "F14", {"entities" : qUnion([Q0, Q1, Q2, Q3, Q4, Q5]), "radius" : 3 * mm, "tangentPropagation" : true, "allowEdgeOverflow" : false});
        }
        {
            var Q0;
            Q0=makeQuery(id+"F1.opExtrude","CAP_EDGE",EDGE,{"disambiguationData":[OSD([sQuery(id+"F0.wireOp",EDGE,"E1.bottom")])],"isStart":false});
            fillet(context, id + "F15", {"entities" : qUnion([Q0]), "radius" : 2 * mm, "tangentPropagation" : true, "allowEdgeOverflow" : false});
        }
        {
            var Q0;
            {var subQ0=sQuery(id+"F0.wireOp",EDGE,"E22.filletArc");var subQ1=sQuery(id+"F0.wireOp",EDGE,"E7");var subQ2=sQuery(id+"F0.wireOp",EDGE,"E6");var subQ3=sQuery(id+"F0.wireOp",EDGE,"E5");var subQ4=sQuery(id+"F0.wireOp",EDGE,"E4");var subQ5=sQuery(id+"F0.wireOp",EDGE,"E1.bottom");var subQ6=sQuery(id+"F0.wireOp",EDGE,"E21.filletArc");var subQ7=sQuery(id+"F0.wireOp",EDGE,"E1.top");var subQ8=sQuery(id+"F0.wireOp",EDGE,"E1.left");var subQ9=sQuery(id+"F0.wireOp",EDGE,"E1.right");var subQ10=sQuery(id+"F0.wireOp",EDGE,"E23.filletArc");var subQ11=sQuery(id+"F0.wireOp",EDGE,"E24.filletArc");Q0=makeQuery(id+"F2.boolean.opBoolean","SPLIT",FACE,{"disambiguationData":[TD([makeQuery(id+"F1.opExtrude","SWEPT_FACE",FACE,{"disambiguationData":[OSD([subQ5])]})])],"derivedFrom":makeQuery(id+"F1.opExtrude","CAP_FACE",FACE,{"disambiguationData":[OSD([subQ5,subQ7,subQ8,subQ9,subQ4,subQ3,subQ2,subQ1,subQ6,subQ0,subQ10,subQ11])],"isStart":true})});}
            var sketch = newSketch(context, id + "F16", { "sketchPlane" : qUnion([Q0])});
            skLineSegment(sketch, "E79", {"start": v(0, 74.25) * mm, "end": v(0, 104.25) * mm});
            skLineSegment(sketch, "E80", {"start": v(0, 104.25) * mm, "end": v(0, 74.25) * mm, "construction": true});
            skCircle(sketch, "E81", {"center": v(0, 104.25) * mm, "radius": 6 * mm});
            skLineSegment(sketch, "E82", {"start": v(-33, 74.25) * mm, "end": v(-15, 92.25) * mm});
            skLineSegment(sketch, "E83", {"start": v(-15, 92.25) * mm, "end": v(-15, 104.25) * mm});
            skArc(sketch, "E84", {"start": v(15, 104.25) * mm, "mid": v(0, 119.25) * mm, "end": v(-15, 104.25) * mm});
            skLineSegment(sketch, "E85", {"start": v(15, 104.25) * mm, "end": v(15, 92.25) * mm});
            skLineSegment(sketch, "E86", {"start": v(15, 92.25) * mm, "end": v(33, 74.25) * mm});
            skLineSegment(sketch, "E87.MirrorCS", {"start": v(15, -92.25) * mm, "end": v(33, -74.25) * mm});
            skArc(sketch, "E88.MirrorCS", {"start": v(15, -104.25) * mm, "mid": v(0, -119.25) * mm, "end": v(-15, -104.25) * mm});
            skLineSegment(sketch, "E89.MirrorCS", {"start": v(-15, -92.25) * mm, "end": v(-15, -104.25) * mm});
            skLineSegment(sketch, "E90.MirrorCS", {"start": v(-33, -74.25) * mm, "end": v(-15, -92.25) * mm});
            skLineSegment(sketch, "E91.MirrorCS", {"start": v(15, -104.25) * mm, "end": v(15, -92.25) * mm});
            skCircle(sketch, "E92.MirrorC", {"center": v(0, -104.25) * mm, "radius": 6 * mm});
            skSolve(sketch);
        }
        {
            var Q0;
            Q0=makeQuery(id+"F16.imprint","IMPRINT",FACE,{"disambiguationData":[TD([[makeQuery(id+"F16.imprint","IMPRINT",EDGE,{"derivedFrom":sQuery(id+"F16.wireOp",EDGE,"E81")}),-1.0]])]});
            var Q1;
            Q1=makeQuery(id+"F16.imprint","IMPRINT",FACE,{"disambiguationData":[TD([[makeQuery(id+"F16.imprint","IMPRINT",EDGE,{"derivedFrom":makeQuery(id+"F1.opExtrude","CAP_EDGE",EDGE,{"disambiguationData":[OSD([sQuery(id+"F0.wireOp",EDGE,"E1.left")])],"isStart":true})}),-1.0]])]});
            var Q2;
            {var subQ1=sQuery(id+"F16.wireOp",EDGE,"E87.MirrorCS");Q2=makeQuery(id+"F16.imprint","IMPRINT",FACE,{"disambiguationData":[TD([[makeQuery(id+"F16.imprint","IMPRINT",EDGE,{"derivedFrom":subQ1}),1.0]])]});}
            var Q3;
            Q3=makeQuery(id+"F2.opExtrude","CAP_FACE",FACE,{"disambiguationData":[OSD([sQuery(id+"F0.wireOp",EDGE,"E12"),sQuery(id+"F0.wireOp",EDGE,"E13"),sQuery(id+"F0.wireOp",EDGE,"E14"),sQuery(id+"F0.wireOp",EDGE,"E15"),sQuery(id+"F0.wireOp",EDGE,"E17.filletArc"),sQuery(id+"F0.wireOp",EDGE,"E18.filletArc"),sQuery(id+"F0.wireOp",EDGE,"E19.filletArc"),sQuery(id+"F0.wireOp",EDGE,"E20.filletArc"),sQuery(id+"F0.wireOp",EDGE,"E25.0"),sQuery(id+"F0.wireOp",EDGE,"E25.1"),sQuery(id+"F0.wireOp",EDGE,"E25.2"),sQuery(id+"F0.wireOp",EDGE,"E25.3"),sQuery(id+"F0.wireOp",EDGE,"E25.4"),sQuery(id+"F0.wireOp",EDGE,"E25.5"),sQuery(id+"F0.wireOp",EDGE,"E25.6"),sQuery(id+"F0.wireOp",EDGE,"E25.7")])],"isStart":false});
            extrude(context, id + "F17", {"entities" : qUnion([Q0, Q1, Q2]), "operationType" : NewBodyOperationType.ADD, "endBound" : BoundingType.UP_TO_SURFACE, "endBoundEntityFace" : qUnion([Q3]), "depth" : 25 * mm});
        }
    });
